# Revit family: Scale-SR_Scales-SR555i
name_source: partatom
category: Specialty Equipment
units: mm (PartAtom-declared; Revit-internal decimal feet)

## family parameters
Always vertical = Yes
Cut with Voids When Loaded = No
OmniClass Number = 23.40.70.11.14.11
OmniClass Title = Medical Equipment
Part Type = Normal
Room Calculation Point = No
Round Connector Dimension = Use Diameter
Shared = No
Work Plane-Based = No

## types (5) — shared parameters
Accuracy = 0.1% +/- 1 Digit of Displayed Resolution
Assembly Code = E1020810
Auto Power Down = 30 to 300 Seconds
Auto Zero = One Button Operation
Averaging = Automatic Digital Filter
BIM Version = v3.1
BIM Version Available (Earliest) = 2017
Calibration = Traceable to NIST Standards
Default Elevation = 0"
Display Resolution = 0.1 lb / 0.1 kg
Display Type = 16-Character Dot-Matrix LCD
Enter = Stores Displayed Reading in Memory
Integrated Height Gauge = Telescoping - 43'' to 78''
Manufacturer = SR Scales by SR Instruments, Inc.
Maximum Weight Capacity = 1000 lbs or 454 kg
Optional Hand Rails Part Number = SR3070
Optional Height Rod Part Number = SR3086
Platform Depth = 18 1/2"
Platform Size = 15 3/4'' x 18 1/2'' (40 cm x 47 cm)
Platform Width = 15 3/4"
Power Supply = Six (6) ''C'' Cell Batteries
Product Page URL = https://srinstruments.com
Recall = Recalls Last Stored Stable Weight, Height and BMI
URL = http://www.srinstruments.com

## per-type parameters (varying)
| type | Description | Show Handrails | Show Height Rod |
| SR555i | Digital Stand-On Scale | No | No |
| SR555i-HBHR (SR3086 SR3070) | Digital Stand-On Scale with Height Bar and Handrails | Yes | Yes |
| SR555i-HB (SR3086) | Digital Stand-On Scale with Height Bar | No | Yes |
| SR555i-HR (SR3070) | Digital Stand-On Scale with Handrails | Yes | No |
| SR555i-KG | Digital Stand-On Scale - KG Only | No | No |

note: column(s) folded — value = type name in every type: Model

## geometry (parser evidence)
native form markers: Blend x2, Sweep x3
no freeform markers — native parametric forms only
